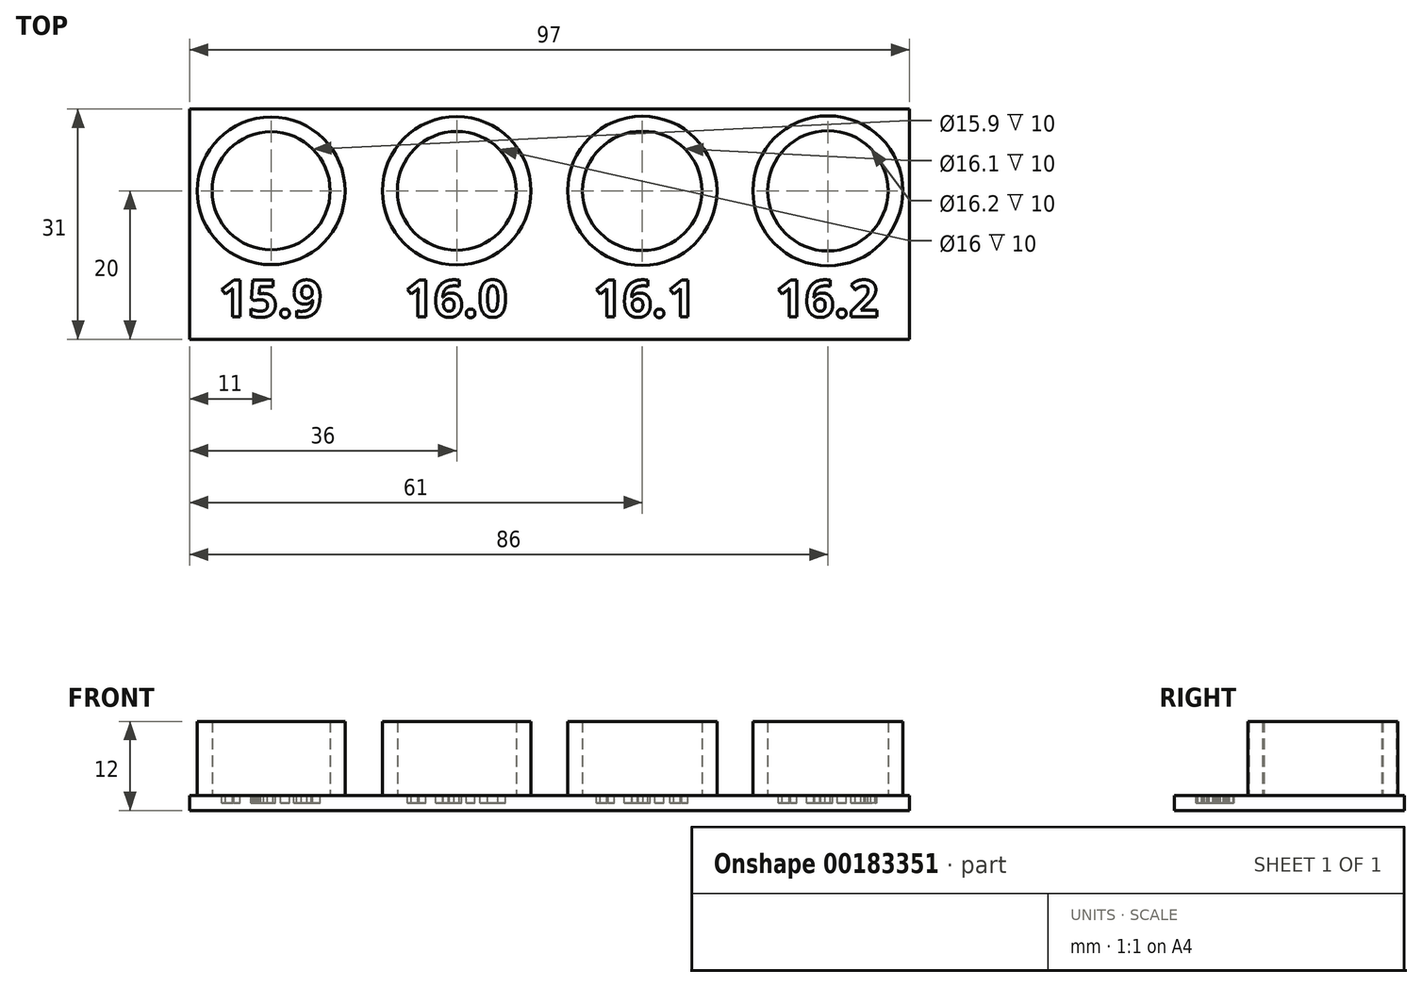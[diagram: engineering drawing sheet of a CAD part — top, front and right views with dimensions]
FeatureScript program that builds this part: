
annotation { "Feature Type Name" : "Feature", "Feature Type Description" : "" }
export const myFeature = defineFeature(function(context is Context, id is Id, definition is map)
    precondition{}
    {
        {
            var Q0;
            Q0=qCreatedBy(makeId("Top.planeOp"),FACE);
            var sketch = newSketch(context, id + "F0", { "sketchPlane" : qUnion([Q0])});
            skCircle(sketch, "E0", {"center": v(-50, 0) * mm, "radius": 8 * mm});
            skCircle(sketch, "E1", {"center": v(-50, 0) * mm, "radius": 10 * mm});
            skCircle(sketch, "E2", {"center": v(-25, 0) * mm, "radius": 8.05 * mm});
            skCircle(sketch, "E3", {"center": v(-25, 0) * mm, "radius": 10.05 * mm});
            skCircle(sketch, "E4", {"center": v(0, 0) * mm, "radius": 8.1 * mm});
            skCircle(sketch, "E5", {"center": v(0, 0) * mm, "radius": 10.1 * mm});
            skCircle(sketch, "E6", {"center": v(-75, 0) * mm, "radius": 7.95 * mm});
            skCircle(sketch, "E7", {"center": v(-75, 0) * mm, "radius": 9.95 * mm});
            skSolve(sketch);
        }
        {
            var Q0;
            Q0=makeQuery(id+"F0.imprint","IMPRINT",FACE,{"disambiguationData":[TD([[makeQuery(id+"F0.imprint","IMPRINT",EDGE,{"derivedFrom":sQuery(id+"F0.wireOp",EDGE,"E6")}),-1.0]])]});
            var Q1;
            Q1=makeQuery(id+"F0.imprint","IMPRINT",FACE,{"disambiguationData":[TD([[makeQuery(id+"F0.imprint","IMPRINT",EDGE,{"derivedFrom":sQuery(id+"F0.wireOp",EDGE,"E0")}),-1.0]])]});
            var Q2;
            Q2=makeQuery(id+"F0.imprint","IMPRINT",FACE,{"disambiguationData":[TD([[makeQuery(id+"F0.imprint","IMPRINT",EDGE,{"derivedFrom":sQuery(id+"F0.wireOp",EDGE,"E2")}),-1.0]])]});
            var Q3;
            Q3=makeQuery(id+"F0.imprint","IMPRINT",FACE,{"disambiguationData":[TD([[makeQuery(id+"F0.imprint","IMPRINT",EDGE,{"derivedFrom":sQuery(id+"F0.wireOp",EDGE,"E4")}),-1.0]])]});
            extrude(context, id + "F1", {"entities" : qUnion([Q0, Q1, Q2, Q3]), "depth" : 10 * mm});
        }
        {
            var Q0;
            Q0=qCreatedBy(makeId("Top.planeOp"),FACE);
            var sketch = newSketch(context, id + "F2", { "sketchPlane" : qUnion([Q0])});
            skLineSegment(sketch, "E8.bottom", {"start": v(-86, 11) * mm, "end": v(11, 11) * mm});
            skLineSegment(sketch, "E8.top", {"start": v(-86, -20) * mm, "end": v(11, -20) * mm});
            skLineSegment(sketch, "E8.left", {"start": v(-86, 11) * mm, "end": v(-86, -20) * mm});
            skLineSegment(sketch, "E8.right", {"start": v(11, 11) * mm, "end": v(11, -20) * mm});
            skSolve(sketch);
        }
        {
            var Q0;
            Q0=makeQuery(id+"F2.imprint","IMPRINT",FACE,{"disambiguationData":[TD([[makeQuery(id+"F2.imprint","IMPRINT",EDGE,{"derivedFrom":sQuery(id+"F2.wireOp",EDGE,"E8.bottom")}),-1.0]])]});
            extrude(context, id + "F3", {"entities" : qUnion([Q0]), "oppositeDirection" : true, "depth" : 2 * mm});
        }
        {
            var Q0;
            Q0=makeQuery(id+"F1.opExtrude","SWEPT_BODY",BODY,{"disambiguationData":[OSD([sQuery(id+"F0.wireOp",EDGE,"E6"),sQuery(id+"F0.wireOp",EDGE,"E7")])]});
            var Q1;
            Q1=makeQuery(id+"F1.opExtrude","SWEPT_BODY",BODY,{"disambiguationData":[OSD([sQuery(id+"F0.wireOp",EDGE,"E0"),sQuery(id+"F0.wireOp",EDGE,"E1")])]});
            var Q2;
            Q2=makeQuery(id+"F1.opExtrude","SWEPT_BODY",BODY,{"disambiguationData":[OSD([sQuery(id+"F0.wireOp",EDGE,"E2"),sQuery(id+"F0.wireOp",EDGE,"E3")])]});
            var Q3;
            Q3=makeQuery(id+"F1.opExtrude","SWEPT_BODY",BODY,{"disambiguationData":[OSD([sQuery(id+"F0.wireOp",EDGE,"E4"),sQuery(id+"F0.wireOp",EDGE,"E5")])]});
            var Q4;
            Q4=makeQuery(id+"F3.opExtrude","SWEPT_BODY",BODY,{"disambiguationData":[OSD([sQuery(id+"F2.wireOp",EDGE,"E8.bottom"),sQuery(id+"F2.wireOp",EDGE,"E8.top"),sQuery(id+"F2.wireOp",EDGE,"E8.left"),sQuery(id+"F2.wireOp",EDGE,"E8.right")])]});
            booleanBodies(context, id + "F4", {"operationType" : BooleanOperationType.UNION, "tools" : qUnion([Q0, Q1, Q2, Q3, Q4])});
        }
        {
            var Q0;
            {var subQ0=sQuery(id+"F2.wireOp",EDGE,"E8.top");var subQ1=sQuery(id+"F2.wireOp",EDGE,"E8.bottom");var subQ2=sQuery(id+"F2.wireOp",EDGE,"E8.left");var subQ3=sQuery(id+"F2.wireOp",EDGE,"E8.right");Q0=makeQuery(id+"F4.opBoolean","SPLIT",FACE,{"disambiguationData":[TD([makeQuery(id+"F1.opExtrude","SWEPT_FACE",FACE,{"disambiguationData":[OSD([sQuery(id+"F0.wireOp",EDGE,"E1")])]})])],"derivedFrom":makeQuery(id+"F3.opExtrude","CAP_FACE",FACE,{"disambiguationData":[OSD([subQ1,subQ0,subQ2,subQ3])],"isStart":true})});}
            var sketch = newSketch(context, id + "F5", { "sketchPlane" : qUnion([Q0])});
            skText(sketch, "E9", { "text": "16.1", "fontName": "OpenSans-Bold.ttf"});
            skText(sketch, "E10", { "text": "16.2", "fontName": "OpenSans-Bold.ttf"});
            skText(sketch, "E11", { "text": "15.9", "fontName": "OpenSans-Bold.ttf"});
            skText(sketch, "E12", { "text": "16.0", "fontName": "OpenSans-Bold.ttf"});
            const initialGuessF5  = {"E9": [-0.03161, -0.017, 1, 0, 0.005], "E10": [-0.00705, -0.017, 1, 0, 0.005], "E11": [-0.08204, -0.017, 1, 0, 0.005], "E12": [-0.05704, -0.017, 1, 0, 0.005]};
            skSetInitialGuess(sketch, initialGuessF5);
            skSolve(sketch);
        }
        {
            var Q0;
            Q0 = qSketchRegion(id + "F5", true);
            extrude(context, id + "F6", {"entities" : qUnion([Q0]), "operationType" : NewBodyOperationType.REMOVE, "oppositeDirection" : true, "depth" : 1 * mm});
        }
    });
